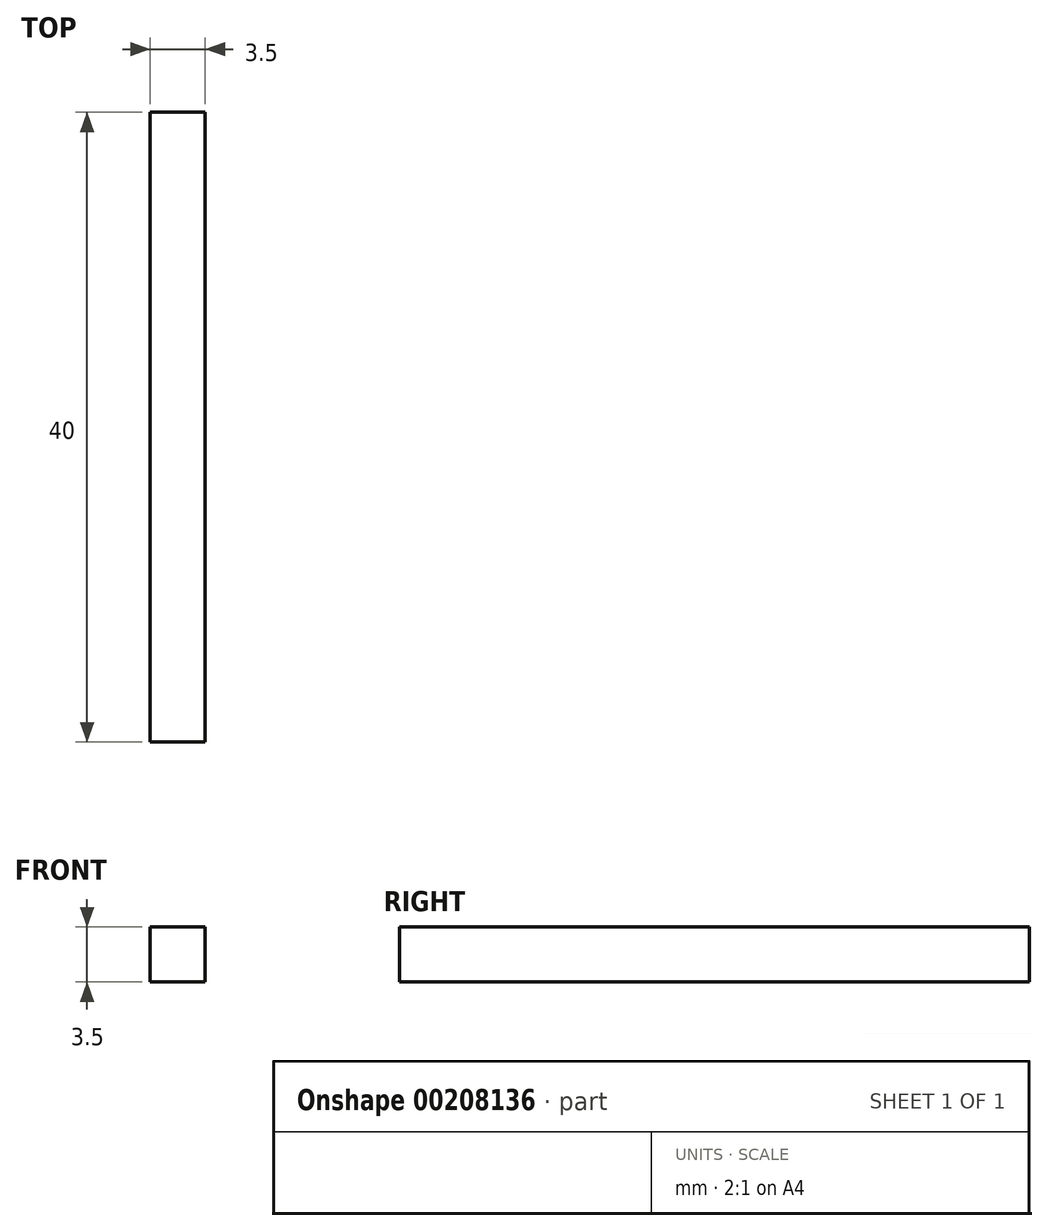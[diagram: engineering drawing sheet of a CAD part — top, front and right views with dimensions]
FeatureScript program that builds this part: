
annotation { "Feature Type Name" : "Feature", "Feature Type Description" : "" }
export const myFeature = defineFeature(function(context is Context, id is Id, definition is map)
    precondition{}
    {
        {
            var Q0;
            Q0=qCreatedBy(makeId("Top.planeOp"),FACE);
            var sketch = newSketch(context, id + "F0", { "sketchPlane" : qUnion([Q0])});
            skLineSegment(sketch, "E0.bottom", {"start": v(1.75, -20) * mm, "end": v(-1.75, -20) * mm});
            skLineSegment(sketch, "E0.top", {"start": v(1.75, 20) * mm, "end": v(-1.75, 20) * mm});
            skLineSegment(sketch, "E0.left", {"start": v(1.75, -20) * mm, "end": v(1.75, 20) * mm});
            skLineSegment(sketch, "E0.right", {"start": v(-1.75, -20) * mm, "end": v(-1.75, 20) * mm});
            skPoint(sketch, "E0.middle", {"position": v(0, 0) * mm});
            skSolve(sketch);
        }
        {
            var Q0;
            Q0 = qSketchRegion(id + "F0", true);
            extrude(context, id + "F1", {"entities" : qUnion([Q0]), "depth" : 3.5 * mm});
        }
    });
